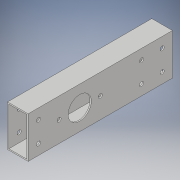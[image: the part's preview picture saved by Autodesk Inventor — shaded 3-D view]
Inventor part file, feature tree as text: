
AUTODESK INVENTOR PART (.ipt)
format: ipt  version: 2018 (Build 220112000, 112)  size: 141,824 bytes
history: native  units: in
note: dims shown in document units (in); Inventor stores cm internally (conversion verified against a paired STEP export)
features: hole x7, extrude x2, sketch x2, shell x1
ambient origin geometry x8: Origin, YZ Plane, XZ Plane, XY Plane, X Axis, Y Axis, Z Axis, Center Point
bodies: Solid1 (feature_tree)
feature tree (12):
  extrude  "Extrusion1"  Depth=2.0in
  shell  "Shell1"  Thickness=7.0in
  hole  "Hole1"  [1 undecoded]
  extrude  "Extrusion2"  Depth=1.0in
  hole  "Hole2"  [1 undecoded]
  hole  "Hole3"  [1 undecoded]
  hole  "Hole4"  [1 undecoded]
  hole  "Hole5"  [1 undecoded]
  hole  "Hole6"  [1 undecoded]
  hole  "Hole7"  [1 undecoded]
  sketch  "Sketch1"  dims[d0=1.0in d1=2.0in d2=7.0in d3=0.0in]
  sketch  "Sketch2"  dims[d4=0.0625in d5=1.0in d6=2.5in d7=1.125in d8=0.75in d9=0.375in d10=0.25in d11=0.5635in d12=1.0in d13=0.8108in d14=2.5in d16=1.0in d17=1.0in d18=0.2031in d19=0.2031in d20=7.0in d21=0.0in d22=0.5in d23=0.5in d24=0.2031in d25=0.75in d26=0.375in d27=0.25in d28=0.5635in d29=1.0in d30=0.8108in d31=0.5in d32=0.5in d33=0.2031in d34=0.75in d35=0.375in d36=0.25in d37=0.5635in d38=1.0in d39=0.8108in d40=0.5in d41=0.5in d42=0.2031in d43=0.75in d44=0.375in d45=0.25in d46=0.5635in d47=1.0in d48=0.8108in d49=0.5in d50=1.5in d51=0.2031in d52=0.75in d53=0.375in d54=0.25in d55=0.5635in d56=1.0in d57=0.8108in d58=0.5in d59=1.5in d60=0.2031in d61=0.75in d62=0.375in d63=0.25in d64=0.5635in d65=1.0in d66=0.8108in d67=0.5in d68=0.5in d69=0.2031in d70=0.75in d71=0.375in d72=0.25in d73=0.5635in d74=1.0in d75=0.8108in]
note: 7 required parameter values undecoded (feature->parameter linkage not recoverable at this tier; creation-order binding heuristic only, values carry confidence <= 0.55)
